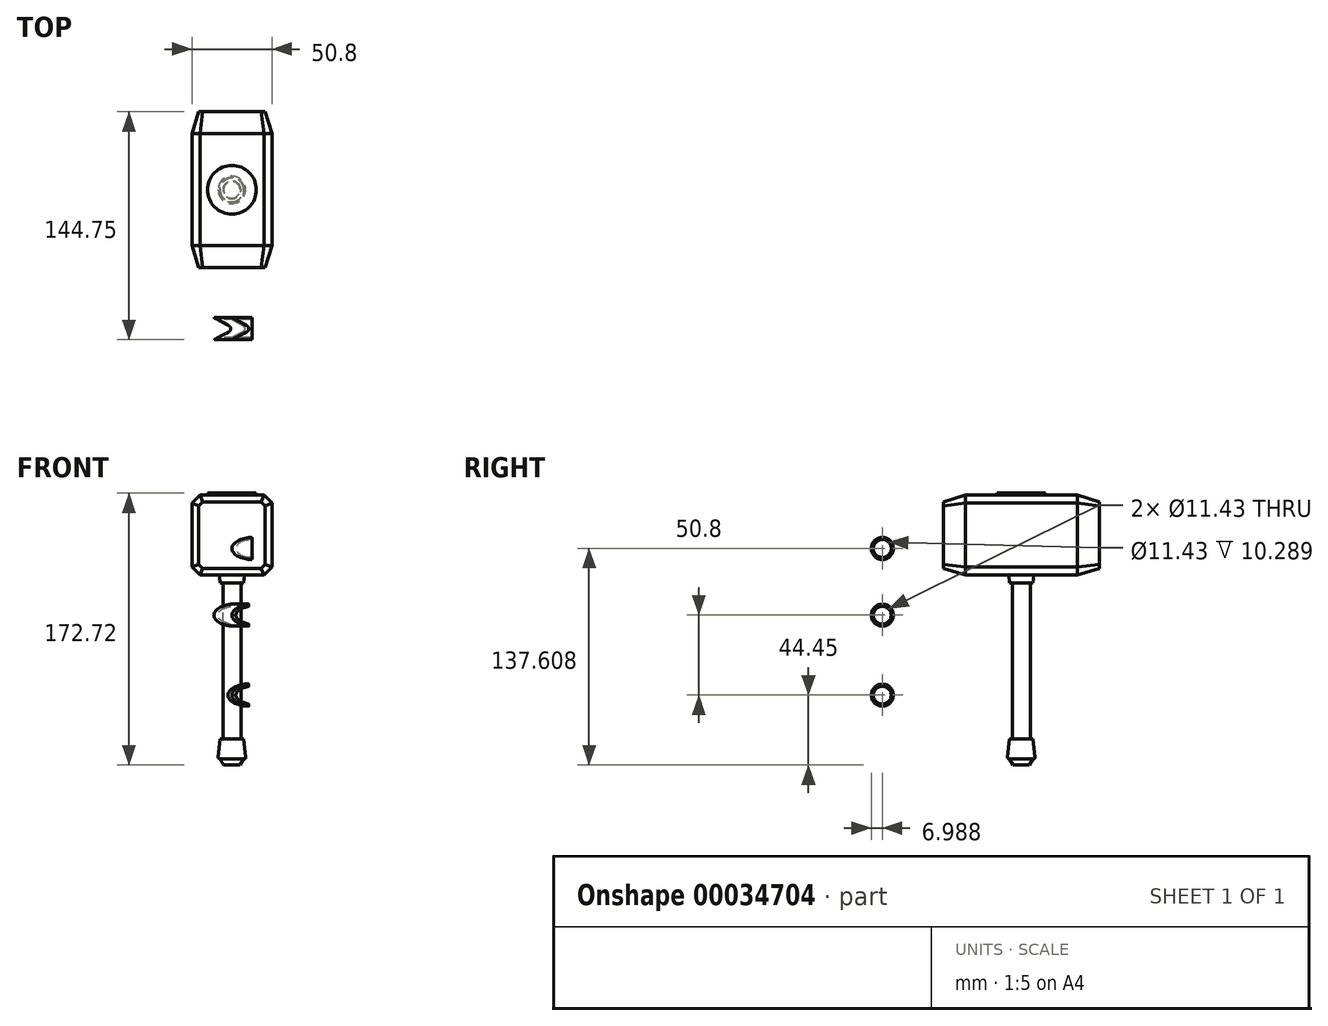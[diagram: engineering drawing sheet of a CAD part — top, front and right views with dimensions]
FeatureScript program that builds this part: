
annotation { "Feature Type Name" : "Feature", "Feature Type Description" : "" }
export const myFeature = defineFeature(function(context is Context, id is Id, definition is map)
    precondition{}
    {
        {
            var Q0;
            Q0=qCreatedBy(makeId("Front.planeOp"),FACE);
            var sketch = newSketch(context, id + "F0", { "sketchPlane" : qUnion([Q0])});
            skLineSegment(sketch, "E0.rect.bottom", {"start": v(25.4, 25.4) * mm, "end": v(-25.4, 25.4) * mm});
            skLineSegment(sketch, "E0.rect.top", {"start": v(25.4, -25.4) * mm, "end": v(-25.4, -25.4) * mm});
            skLineSegment(sketch, "E0.rect.left", {"start": v(25.4, 25.4) * mm, "end": v(25.4, -25.4) * mm});
            skLineSegment(sketch, "E0.rect.right", {"start": v(-25.4, 25.4) * mm, "end": v(-25.4, -25.4) * mm});
            skPoint(sketch, "E0.rect.middle", {"position": v(0, 0) * mm});
            skSolve(sketch);
        }
        {
            var Q0;
            Q0=makeQuery(id+"F0.imprint","IMPRINT",FACE,{"disambiguationData":[TD([[makeQuery(id+"F0.imprint","IMPRINT",EDGE,{"derivedFrom":sQuery(id+"F0.wireOp",EDGE,"E0.rect.bottom")}),1.0]])]});
            extrude(context, id + "F1", {"entities" : qUnion([Q0]), "endBound" : BoundingType.SYMMETRIC, "depth" : 71.12 * mm});
        }
        {
            var Q0;
            Q0=makeQuery(id+"F1.opExtrude","SWEPT_EDGE",EDGE,{"disambiguationData":[OSD([sQuery(id+"F0.wireOp",EDGE,"E0.rect.bottom"),sQuery(id+"F0.wireOp",EDGE,"E0.rect.left")])]});
            var Q1;
            Q1=makeQuery(id+"F1.opExtrude","SWEPT_EDGE",EDGE,{"disambiguationData":[OSD([sQuery(id+"F0.wireOp",EDGE,"E0.rect.top"),sQuery(id+"F0.wireOp",EDGE,"E0.rect.left")])]});
            var Q2;
            Q2=makeQuery(id+"F1.opExtrude","SWEPT_EDGE",EDGE,{"disambiguationData":[OSD([sQuery(id+"F0.wireOp",EDGE,"E0.rect.top"),sQuery(id+"F0.wireOp",EDGE,"E0.rect.right")])]});
            var Q3;
            Q3=makeQuery(id+"F1.opExtrude","SWEPT_EDGE",EDGE,{"disambiguationData":[OSD([sQuery(id+"F0.wireOp",EDGE,"E0.rect.bottom"),sQuery(id+"F0.wireOp",EDGE,"E0.rect.right")])]});
            chamfer(context, id + "F2", {"entities" : qUnion([Q0, Q1, Q2, Q3]), "width" : 5.08 * mm, "tangentPropagation" : true});
        }
        {
            var Q0;
            Q0=makeQuery(id+"F1.opExtrude","CAP_FACE",FACE,{"disambiguationData":[OSD([sQuery(id+"F0.wireOp",EDGE,"E0.rect.bottom"),sQuery(id+"F0.wireOp",EDGE,"E0.rect.top"),sQuery(id+"F0.wireOp",EDGE,"E0.rect.left"),sQuery(id+"F0.wireOp",EDGE,"E0.rect.right")])],"isStart":false});
            var sketch = newSketch(context, id + "F3", { "sketchPlane" : qUnion([Q0])});
            skLineSegment(sketch, "E1.0.0", {"start": v(20.32, 25.4) * mm, "end": v(-20.32, 25.4) * mm});
            skLineSegment(sketch, "E1.0.1", {"start": v(-20.32, 25.4) * mm, "end": v(-25.4, 20.32) * mm});
            skLineSegment(sketch, "E1.0.2", {"start": v(-25.4, 20.32) * mm, "end": v(-25.4, -20.32) * mm});
            skLineSegment(sketch, "E1.0.3", {"start": v(-25.4, -20.32) * mm, "end": v(-20.32, -25.4) * mm});
            skLineSegment(sketch, "E1.0.4", {"start": v(-20.32, -25.4) * mm, "end": v(20.32, -25.4) * mm});
            skLineSegment(sketch, "E1.0.5", {"start": v(20.32, -25.4) * mm, "end": v(25.4, -20.32) * mm});
            skLineSegment(sketch, "E1.0.6", {"start": v(25.4, -20.32) * mm, "end": v(25.4, 20.32) * mm});
            skLineSegment(sketch, "E1.0.7", {"start": v(25.4, 20.32) * mm, "end": v(20.32, 25.4) * mm});
            skSolve(sketch);
        }
        {
            var Q0;
            Q0=makeQuery(id+"F1.opExtrude","CAP_FACE",FACE,{"disambiguationData":[OSD([sQuery(id+"F0.wireOp",EDGE,"E0.rect.bottom"),sQuery(id+"F0.wireOp",EDGE,"E0.rect.top"),sQuery(id+"F0.wireOp",EDGE,"E0.rect.left"),sQuery(id+"F0.wireOp",EDGE,"E0.rect.right")])],"isStart":false});
            var Q1;
            Q1=makeQuery(id+"F3.imprint","IMPRINT",FACE,{"disambiguationData":[TD([[makeQuery(id+"F3.imprint","IMPRINT",EDGE,{"derivedFrom":sQuery(id+"F3.wireOp",EDGE,"E1.0.0")}),1.0]])]});
            extrude(context, id + "F4", {"entities" : qUnion([Q0, Q1]), "operationType" : NewBodyOperationType.ADD, "depth" : 13.97 * mm, "hasDraft" : true, "draftAngle" : 17 * degree, "draftPullDirection" : true});
        }
        {
            var Q0;
            Q0=makeQuery(id+"F1.opExtrude","CAP_FACE",FACE,{"disambiguationData":[OSD([sQuery(id+"F0.wireOp",EDGE,"E0.rect.bottom"),sQuery(id+"F0.wireOp",EDGE,"E0.rect.top"),sQuery(id+"F0.wireOp",EDGE,"E0.rect.left"),sQuery(id+"F0.wireOp",EDGE,"E0.rect.right")])],"isStart":true});
            var sketch = newSketch(context, id + "F5", { "sketchPlane" : qUnion([Q0])});
            skLineSegment(sketch, "E2.0.0", {"start": v(25.4, -20.32) * mm, "end": v(25.4, 20.32) * mm});
            skLineSegment(sketch, "E2.0.1", {"start": v(25.4, 20.32) * mm, "end": v(20.32, 25.4) * mm});
            skLineSegment(sketch, "E2.0.2", {"start": v(20.32, 25.4) * mm, "end": v(-20.32, 25.4) * mm});
            skLineSegment(sketch, "E2.0.3", {"start": v(-20.32, 25.4) * mm, "end": v(-25.4, 20.32) * mm});
            skLineSegment(sketch, "E2.0.4", {"start": v(-25.4, 20.32) * mm, "end": v(-25.4, -20.32) * mm});
            skLineSegment(sketch, "E2.0.5", {"start": v(-25.4, -20.32) * mm, "end": v(-20.32, -25.4) * mm});
            skLineSegment(sketch, "E2.0.6", {"start": v(-20.32, -25.4) * mm, "end": v(20.32, -25.4) * mm});
            skLineSegment(sketch, "E2.0.7", {"start": v(20.32, -25.4) * mm, "end": v(25.4, -20.32) * mm});
            skSolve(sketch);
        }
        {
            var Q0;
            Q0=makeQuery(id+"F5.imprint","IMPRINT",FACE,{"disambiguationData":[TD([[makeQuery(id+"F5.imprint","IMPRINT",EDGE,{"derivedFrom":sQuery(id+"F5.wireOp",EDGE,"E2.0.0")}),-1.0]])]});
            extrude(context, id + "F6", {"entities" : qUnion([Q0]), "operationType" : NewBodyOperationType.ADD, "depth" : 13.97 * mm, "hasDraft" : true, "draftAngle" : 17 * degree, "draftPullDirection" : true});
        }
        {
            var Q0;
            Q0=makeQuery(id+"F1.opExtrude","SWEPT_FACE",FACE,{"disambiguationData":[OSD([sQuery(id+"F0.wireOp",EDGE,"E0.rect.bottom")])]});
            var sketch = newSketch(context, id + "F7", { "sketchPlane" : qUnion([Q0])});
            skCircle(sketch, "E3", {"center": v(0, 0) * mm, "radius": 15.5 * mm});
            skSolve(sketch);
        }
        {
            var Q0;
            Q0 = qSketchRegion(id + "F7", true);
            extrude(context, id + "F8", {"entities" : qUnion([Q0]), "operationType" : NewBodyOperationType.ADD, "depth" : 1.27 * mm});
        }
        {
            var Q0;
            Q0=makeQuery(id+"F1.opExtrude","SWEPT_FACE",FACE,{"disambiguationData":[OSD([sQuery(id+"F0.wireOp",EDGE,"E0.rect.top")])]});
            var sketch = newSketch(context, id + "F9", { "sketchPlane" : qUnion([Q0])});
            skCircle(sketch, "E4", {"center": v(0, 0) * mm, "radius": 7.93 * mm});
            skSolve(sketch);
        }
        {
            var Q0;
            Q0 = qSketchRegion(id + "F9", true);
            extrude(context, id + "F10", {"entities" : qUnion([Q0]), "operationType" : NewBodyOperationType.ADD, "depth" : 5.08 * mm, "hasDraft" : true, "draftAngle" : 5 * degree, "draftPullDirection" : true});
        }
        {
            var Q0;
            Q0=makeQuery(id+"F10.opExtrude","CAP_FACE",FACE,{"disambiguationData":[OSD([sQuery(id+"F9.wireOp",EDGE,"E4")])],"isStart":false});
            var sketch = newSketch(context, id + "F11", { "sketchPlane" : qUnion([Q0])});
            skCircle(sketch, "E5", {"center": v(0, 0) * mm, "radius": 6.99 * mm});
            skCircle(sketch, "E6", {"center": v(0, 0) * mm, "radius": 5.72 * mm});
            skSolve(sketch);
        }
        {
            var Q0;
            Q0=makeQuery(id+"F11.imprint","IMPRINT",FACE,{"disambiguationData":[TD([[makeQuery(id+"F11.imprint","IMPRINT",EDGE,{"derivedFrom":sQuery(id+"F11.wireOp",EDGE,"E6")}),1.0]])]});
            extrude(context, id + "F12", {"entities" : qUnion([Q0]), "operationType" : NewBodyOperationType.ADD, "depth" : 99.06 * mm});
        }
        {
            var Q0;
            Q0=makeQuery(id+"F12.opExtrude","CAP_FACE",FACE,{"disambiguationData":[OSD([sQuery(id+"F11.wireOp",EDGE,"E6")])],"isStart":false});
            var sketch = newSketch(context, id + "F13", { "sketchPlane" : qUnion([Q0])});
            skCircle(sketch, "E7", {"center": v(0, 0) * mm, "radius": 7.55 * mm});
            skSolve(sketch);
        }
        {
            var Q0;
            Q0 = qSketchRegion(id + "F13", true);
            extrude(context, id + "F14", {"entities" : qUnion([Q0]), "depth" : 12.7 * mm, "hasDraft" : true, "draftAngle" : 6 * degree});
        }
        {
            var Q0;
            Q0=makeQuery(id+"F14.opExtrude","CAP_EDGE",EDGE,{"disambiguationData":[OSD([sQuery(id+"F13.wireOp",EDGE,"E7")])],"isStart":false});
            fillet(context, id + "F15", {"entities" : qUnion([Q0]), "radius" : 1.27 * mm, "tangentPropagation" : true, "allowEdgeOverflow" : false});
        }
        {
            var Q0;
            Q0=makeQuery(id+"F14.opExtrude","CAP_FACE",FACE,{"disambiguationData":[OSD([sQuery(id+"F13.wireOp",EDGE,"E7")])],"isStart":false});
            var sketch = newSketch(context, id + "F16", { "sketchPlane" : qUnion([Q0])});
            skCircle(sketch, "E8.0", {"center": v(0, 0) * mm, "radius": 7.47 * mm});
            skSolve(sketch);
        }
        {
            var Q0;
            Q0 = qSketchRegion(id + "F16", true);
            extrude(context, id + "F17", {"entities" : qUnion([Q0]), "operationType" : NewBodyOperationType.ADD, "depth" : 3.8 * mm, "hasDraft" : true, "draftAngle" : 30 * degree, "draftPullDirection" : true});
        }
        {
            var Q0;
            Q0=qCreatedBy(makeId("Right.planeOp"),FACE);
            var sketch = newSketch(context, id + "F18", { "sketchPlane" : qUnion([Q0])});
            skCircle(sketch, "E9", {"center": v(-88.23, -8.44) * mm, "radius": 6.99 * mm});
            skCircle(sketch, "E10", {"center": v(-88.23, -8.44) * mm, "radius": 5.72 * mm});
            skSolve(sketch);
        }
        {
            var Q0;
            Q0 = qSketchRegion(id + "F18", true);
            extrude(context, id + "F19", {"entities" : qUnion([Q0]), "depth" : 12.7 * mm});
        }
        {
            var Q0;
            Q0=qCreatedBy(makeId("Top.planeOp"),FACE);
            var sketch = newSketch(context, id + "F20", { "sketchPlane" : qUnion([Q0])});
            skLineSegment(sketch, "E11.0", {"start": v(12.7, -81.25) * mm, "end": v(12.7, -95.22) * mm});
            skLineSegment(sketch, "E12.0", {"start": v(0, -81.25) * mm, "end": v(0, -88.23) * mm});
            skLineSegment(sketch, "E13", {"start": v(0, -81.25) * mm, "end": v(9.4, -86.15) * mm});
            skLineSegment(sketch, "E14.MirrorCS", {"start": v(0, -95.22) * mm, "end": v(9.4, -90.31) * mm});
            skArc(sketch, "E15", {"start": v(9.4, -90.31) * mm, "mid": v(10.65, -88.23) * mm, "end": v(9.4, -86.15) * mm});
            skPoint(sketch, "E16.orphan", {"position": v(0, -95.22) * mm});
            skLineSegment(sketch, "E17", {"start": v(0, -88.23) * mm, "end": v(0, -95.22) * mm});
            skLineSegment(sketch, "E18", {"start": v(0, -95.22) * mm, "end": v(-11.43, -95.22) * mm});
            skLineSegment(sketch, "E19", {"start": v(0, -81.25) * mm, "end": v(-11.43, -81.25) * mm});
            skLineSegment(sketch, "E20", {"start": v(-11.43, -95.22) * mm, "end": v(-2.04, -90.31) * mm});
            skLineSegment(sketch, "E21", {"start": v(0, -88.23) * mm, "end": v(8.3, -88.23) * mm});
            skLineSegment(sketch, "E22.MirrorCS", {"start": v(-11.43, -81.25) * mm, "end": v(-2.04, -86.15) * mm});
            skArc(sketch, "E23", {"start": v(-2.04, -90.31) * mm, "mid": v(-0.78, -88.23) * mm, "end": v(-2.04, -86.15) * mm});
            skSolve(sketch);
        }
        {
            var Q0;
            Q0 = qSketchRegion(id + "F20", true);
            extrude(context, id + "F21", {"entities" : qUnion([Q0]), "operationType" : NewBodyOperationType.REMOVE, "oppositeDirection" : true, "depth" : 25.4 * mm});
        }
        {
            var Q0;
            Q0=qCreatedBy(makeId("Right.planeOp"),FACE);
            var sketch = newSketch(context, id + "F22", { "sketchPlane" : qUnion([Q0])});
            skCircle(sketch, "E24.0", {"center": v(-88.23, -8.44) * mm, "radius": 5.72 * mm});
            skLineSegment(sketch, "E25", {"start": v(-88.23, -8.44) * mm, "end": v(-88.23, 15.5) * mm});
            skCircle(sketch, "E26", {"center": v(-88.23, 15.5) * mm, "radius": 6.99 * mm});
            skCircle(sketch, "E27", {"center": v(-88.23, 15.5) * mm, "radius": 5.72 * mm});
            skSolve(sketch);
        }
        {
            var Q0;
            Q0=makeQuery(id+"F22.imprint","IMPRINT",FACE,{"disambiguationData":[TD([[makeQuery(id+"F22.imprint","IMPRINT",EDGE,{"derivedFrom":sQuery(id+"F22.wireOp",EDGE,"E26")}),1.0]])]});
            extrude(context, id + "F23", {"entities" : qUnion([Q0]), "endBound" : BoundingType.SYMMETRIC, "depth" : 22.86 * mm});
        }
        {
            var Q0;
            Q0 = qSketchRegion(id + "F20", true);
            extrude(context, id + "F24", {"entities" : qUnion([Q0]), "operationType" : NewBodyOperationType.REMOVE, "endBound" : BoundingType.SYMMETRIC, "oppositeDirection" : true, "depth" : 508 * mm});
        }
        {
            var Q0;
            Q0=makeQuery(id+"F24.boolean.opBoolean","SPLIT",BODY,{"disambiguationData":[OD(0.0)],"derivedFrom":makeQuery(id+"F23.opExtrude","SWEPT_BODY",BODY,{"disambiguationData":[OSD([sQuery(id+"F22.wireOp",EDGE,"E26"),sQuery(id+"F22.wireOp",EDGE,"E27")])]})});
            deleteBodies(context, id + "F25", {"entities" : qUnion([Q0])});
        }
        {
            var Q0;
            Q0=qCreatedBy(makeId("Right.planeOp"),FACE);
            var sketch = newSketch(context, id + "F26", { "sketchPlane" : qUnion([Q0])});
            skCircle(sketch, "E28.0", {"center": v(-88.23, -8.44) * mm, "radius": 5.72 * mm});
            skLineSegment(sketch, "E29", {"start": v(-88.23, -8.44) * mm, "end": v(-88.23, -50.8) * mm});
            skLineSegment(sketch, "E30", {"start": v(0, 0) * mm, "end": v(-109.96, 0) * mm});
            skCircle(sketch, "E31", {"center": v(-88.23, -50.8) * mm, "radius": 6.99 * mm});
            skCircle(sketch, "E32", {"center": v(-88.23, -50.8) * mm, "radius": 5.72 * mm});
            skSolve(sketch);
        }
        {
            var Q0;
            Q0=makeQuery(id+"F26.imprint","IMPRINT",FACE,{"disambiguationData":[TD([[makeQuery(id+"F26.imprint","IMPRINT",EDGE,{"derivedFrom":sQuery(id+"F26.wireOp",EDGE,"E31")}),1.0]])]});
            extrude(context, id + "F27", {"entities" : qUnion([Q0]), "endBound" : BoundingType.SYMMETRIC, "depth" : 25.4 * mm});
        }
        {
            var Q0;
            Q0=qCreatedBy(makeId("Top.planeOp"),FACE);
            cPlane(context, id + "F28", {"entities" : qUnion([Q0]), "cplaneType" : CPlaneType.OFFSET, "offset" : 50.8 * mm, "oppositeDirection" : true, "width" : 152.4 * mm, "height" : 152.4 * mm});
        }
        {
            var Q0;
            Q0=qCreatedBy(id+"F28.planeOp",FACE);
            var sketch = newSketch(context, id + "F29", { "sketchPlane" : qUnion([Q0])});
            skLineSegment(sketch, "E33.0", {"start": v(9.4, -86.15) * mm, "end": v(0, -81.25) * mm});
            skArc(sketch, "E34.0", {"start": v(9.4, -86.15) * mm, "mid": v(10.65, -88.23) * mm, "end": v(9.4, -90.31) * mm});
            skLineSegment(sketch, "E35.0", {"start": v(9.4, -90.31) * mm, "end": v(0, -95.22) * mm});
            skLineSegment(sketch, "E36", {"start": v(12.7, -95.22) * mm, "end": v(0, -95.22) * mm});
            skLineSegment(sketch, "E37.0", {"start": v(12.7, -81.25) * mm, "end": v(12.7, -95.22) * mm});
            skLineSegment(sketch, "E38", {"start": v(0, -81.25) * mm, "end": v(12.7, -81.25) * mm});
            skLineSegment(sketch, "E39.0", {"start": v(-12.7, -81.25) * mm, "end": v(-12.7, -95.22) * mm});
            skArc(sketch, "E40.0", {"start": v(-2.04, -86.15) * mm, "mid": v(-0.78, -88.23) * mm, "end": v(-2.04, -90.31) * mm});
            skLineSegment(sketch, "E41.0", {"start": v(-2.04, -86.15) * mm, "end": v(-11.43, -81.25) * mm});
            skLineSegment(sketch, "E42.0", {"start": v(-2.04, -90.31) * mm, "end": v(-11.43, -95.22) * mm});
            skLineSegment(sketch, "E43", {"start": v(-11.43, -81.25) * mm, "end": v(-12.7, -81.25) * mm});
            skLineSegment(sketch, "E44", {"start": v(-11.43, -95.22) * mm, "end": v(-12.7, -95.22) * mm});
            skSolve(sketch);
        }
        {
            var Q0;
            Q0 = qSketchRegion(id + "F29", true);
            extrude(context, id + "F30", {"entities" : qUnion([Q0]), "operationType" : NewBodyOperationType.REMOVE, "endBound" : BoundingType.SYMMETRIC, "oppositeDirection" : true, "depth" : 25.4 * mm});
        }
        {
            var Q0;
            Q0=qCreatedBy(makeId("Right.planeOp"),FACE);
            var sketch = newSketch(context, id + "F31", { "sketchPlane" : qUnion([Q0])});
            skArc(sketch, "E45.0", {"start": v(-86.15, -56.12) * mm, "mid": v(-82.52, -50.8) * mm, "end": v(-86.15, -45.48) * mm});
            skLineSegment(sketch, "E46", {"start": v(-88.23, -50.8) * mm, "end": v(-88.23, -101.6) * mm});
            skCircle(sketch, "E47", {"center": v(-88.23, -101.6) * mm, "radius": 6.99 * mm});
            skCircle(sketch, "E48", {"center": v(-88.23, -101.6) * mm, "radius": 5.72 * mm});
            skSolve(sketch);
        }
        {
            var Q0;
            Q0=makeQuery(id+"F31.imprint","IMPRINT",FACE,{"disambiguationData":[TD([[makeQuery(id+"F31.imprint","IMPRINT",EDGE,{"derivedFrom":sQuery(id+"F31.wireOp",EDGE,"E47")}),1.0]])]});
            extrude(context, id + "F32", {"entities" : qUnion([Q0]), "endBound" : BoundingType.SYMMETRIC, "depth" : 25.4 * mm});
        }
        {
            var Q0;
            Q0=qCreatedBy(id+"F28.planeOp",FACE);
            cPlane(context, id + "F33", {"entities" : qUnion([Q0]), "cplaneType" : CPlaneType.OFFSET, "offset" : 50.8 * mm, "oppositeDirection" : true, "width" : 152.4 * mm, "height" : 152.4 * mm});
        }
        {
            var Q0;
            Q0=qCreatedBy(id+"F33.planeOp",FACE);
            var sketch = newSketch(context, id + "F34", { "sketchPlane" : qUnion([Q0])});
            skLineSegment(sketch, "E49.0", {"start": v(9.4, -86.15) * mm, "end": v(0, -81.25) * mm});
            skArc(sketch, "E50.0", {"start": v(9.4, -86.15) * mm, "mid": v(10.65, -88.23) * mm, "end": v(9.4, -90.31) * mm});
            skLineSegment(sketch, "E51.0", {"start": v(9.4, -90.31) * mm, "end": v(0, -95.22) * mm});
            skLineSegment(sketch, "E52", {"start": v(-2.54, -95.22) * mm, "end": v(-2.54, -81.25) * mm});
            skLineSegment(sketch, "E53", {"start": v(-2.54, -95.22) * mm, "end": v(6.85, -90.31) * mm});
            skLineSegment(sketch, "E54.MirrorCS", {"start": v(-2.54, -81.25) * mm, "end": v(6.85, -86.15) * mm});
            skPoint(sketch, "E55.end.orphan", {"position": v(-2.54, -88.23) * mm});
            skArc(sketch, "E56", {"start": v(6.85, -90.31) * mm, "mid": v(8.11, -88.23) * mm, "end": v(6.85, -86.15) * mm});
            skLineSegment(sketch, "E57", {"start": v(-2.54, -95.22) * mm, "end": v(-16.11, -102.03) * mm});
            skLineSegment(sketch, "E58", {"start": v(-16.11, -102.03) * mm, "end": v(-15.24, -76.78) * mm});
            skLineSegment(sketch, "E59", {"start": v(-15.24, -76.78) * mm, "end": v(-2.54, -81.25) * mm});
            skLineSegment(sketch, "E60", {"start": v(0, -95.22) * mm, "end": v(15.67, -96.34) * mm});
            skLineSegment(sketch, "E61", {"start": v(15.67, -96.34) * mm, "end": v(14.05, -78.86) * mm});
            skLineSegment(sketch, "E62", {"start": v(14.05, -78.86) * mm, "end": v(0, -81.25) * mm});
            skSolve(sketch);
        }
        {
            var Q0;
            Q0 = qSketchRegion(id + "F34", true);
            extrude(context, id + "F35", {"entities" : qUnion([Q0]), "operationType" : NewBodyOperationType.REMOVE, "endBound" : BoundingType.SYMMETRIC, "oppositeDirection" : true, "depth" : 25.4 * mm});
        }
    });
